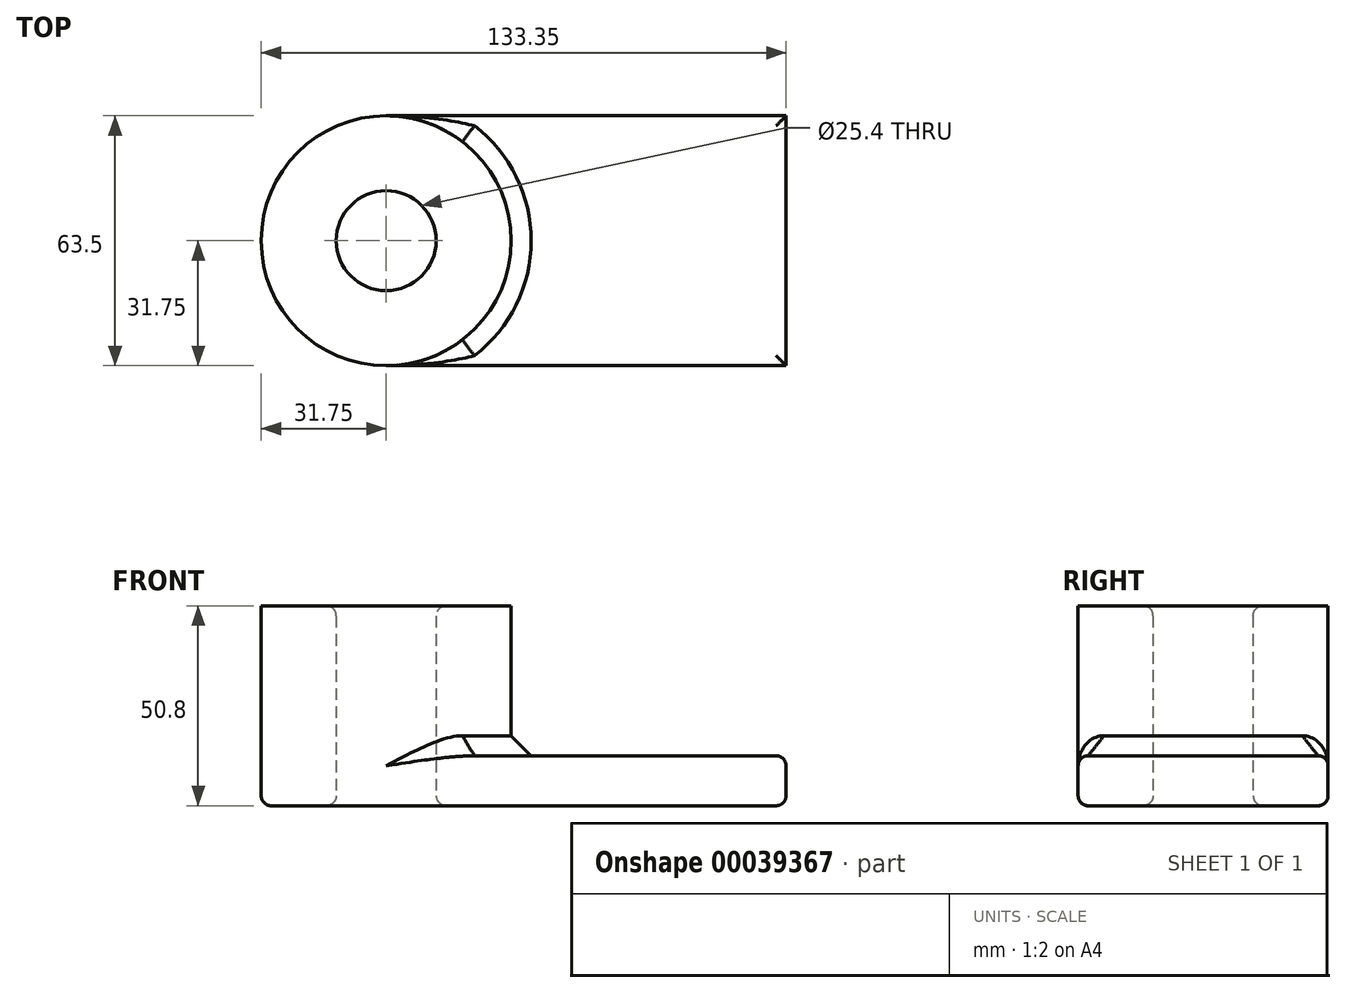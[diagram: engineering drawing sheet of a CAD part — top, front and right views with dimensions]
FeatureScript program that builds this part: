
annotation { "Feature Type Name" : "Feature", "Feature Type Description" : "" }
export const myFeature = defineFeature(function(context is Context, id is Id, definition is map)
    precondition{}
    {
        {
            var Q0;
            Q0=qCreatedBy(makeId("Top.planeOp"),FACE);
            var sketch = newSketch(context, id + "F0", { "sketchPlane" : qUnion([Q0])});
            skLineSegment(sketch, "E0.rect.bottom", {"start": v(50.8, -31.75) * mm, "end": v(-50.8, -31.75) * mm});
            skLineSegment(sketch, "E0.rect.top", {"start": v(50.8, 31.75) * mm, "end": v(-50.8, 31.75) * mm});
            skLineSegment(sketch, "E0.rect.left", {"start": v(50.8, -31.75) * mm, "end": v(50.8, 31.75) * mm});
            skLineSegment(sketch, "E0.rect.right", {"start": v(-50.8, -31.75) * mm, "end": v(-50.8, 31.75) * mm});
            skPoint(sketch, "E0.rect.middle", {"position": v(0, 0) * mm});
            skCircle(sketch, "E1", {"center": v(-50.8, 0) * mm, "radius": 31.75 * mm});
            skCircle(sketch, "E2", {"center": v(-50.8, 0) * mm, "radius": 12.7 * mm});
            skSolve(sketch);
        }
        {
            var Q0;
            {var subQ0=sQuery(id+"F0.wireOp",EDGE,"E2");var subQ1=sQuery(id+"F0.wireOp",EDGE,"E0.rect.right");var subQ3=makeQuery(id+"F0.imprint","INTERSECT",VERTEX,{"disambiguationData":[OD(0.0)],"derivedFrom":[subQ1,subQ0]});Q0=makeQuery(id+"F0.imprint","IMPRINT",FACE,{"disambiguationData":[TD([[makeQuery(id+"F0.imprint","IMPRINT",EDGE,{"disambiguationData":[TD([[subQ3,-1.0]])],"derivedFrom":subQ0}),-1.0]])]});}
            var Q1;
            {var subQ0=sQuery(id+"F0.wireOp",EDGE,"E2");var subQ1=sQuery(id+"F0.wireOp",EDGE,"E0.rect.right");var subQ3=makeQuery(id+"F0.imprint","INTERSECT",VERTEX,{"disambiguationData":[OD(0.0)],"derivedFrom":[subQ1,subQ0]});Q1=makeQuery(id+"F0.imprint","IMPRINT",FACE,{"disambiguationData":[TD([[makeQuery(id+"F0.imprint","IMPRINT",EDGE,{"disambiguationData":[TD([[subQ3,1.0]])],"derivedFrom":subQ0}),-1.0]])]});}
            extrude(context, id + "F1", {"entities" : qUnion([Q0, Q1]), "depth" : 50.8 * mm});
        }
        {
            var Q0;
            Q0 = qSketchRegion(id + "F0", true);
            extrude(context, id + "F2", {"entities" : qUnion([Q0]), "operationType" : NewBodyOperationType.ADD, "depth" : 12.7 * mm});
        }
        {
            var Q0;
            Q0=makeQuery(id+"F1.opExtrude","CAP_EDGE",EDGE,{"disambiguationData":[OSD([sQuery(id+"F0.wireOp",EDGE,"E2")])],"isStart":false});
            var Q1;
            Q1=makeQuery(id+"F2.opExtrude","CAP_EDGE",EDGE,{"disambiguationData":[OSD([sQuery(id+"F0.wireOp",EDGE,"E0.rect.left")])],"isStart":false});
            var Q2;
            Q2=makeQuery(id+"F2.opExtrude","CAP_EDGE",EDGE,{"disambiguationData":[OSD([sQuery(id+"F0.wireOp",EDGE,"E0.rect.bottom")])],"isStart":false});
            var Q3;
            Q3=makeQuery(id+"F1.opExtrude","CAP_EDGE",EDGE,{"disambiguationData":[OSD([sQuery(id+"F0.wireOp",EDGE,"E2")])],"isStart":true});
            var Q4;
            Q4=makeQuery(id+"F1.opExtrude","CAP_EDGE",EDGE,{"disambiguationData":[OSD([sQuery(id+"F0.wireOp",EDGE,"E1")])],"isStart":true});
            var Q5;
            Q5=makeQuery(id+"F2.opExtrude","CAP_EDGE",EDGE,{"disambiguationData":[OSD([sQuery(id+"F0.wireOp",EDGE,"E0.rect.top")])],"isStart":false});
            var Q6;
            Q6=makeQuery(id+"F2.opExtrude","CAP_EDGE",EDGE,{"disambiguationData":[OSD([sQuery(id+"F0.wireOp",EDGE,"E0.rect.left")])],"isStart":true});
            fillet(context, id + "F3", {"entities" : qUnion([Q0, Q1, Q2, Q3, Q4, Q5, Q6]), "radius" : 2.54 * mm, "tangentPropagation" : true, "allowEdgeOverflow" : false});
        }
        {
            var Q0;
            {var subQ0=sQuery(id+"F0.wireOp",EDGE,"E1");Q0=makeQuery(id+"F2.boolean.opBoolean","INTERSECT",EDGE,{"derivedFrom":[makeQuery(id+"F1.opExtrude","SWEPT_FACE",FACE,{"disambiguationData":[OSD([subQ0])]}),makeQuery(id+"F2.opExtrude","CAP_FACE",FACE,{"disambiguationData":[OSD([sQuery(id+"F0.wireOp",EDGE,"E0.rect.bottom"),sQuery(id+"F0.wireOp",EDGE,"E0.rect.top"),sQuery(id+"F0.wireOp",EDGE,"E0.rect.left"),subQ0,sQuery(id+"F0.wireOp",EDGE,"E2")])],"isStart":false})]});}
            chamfer(context, id + "F4", {"entities" : qUnion([Q0]), "width" : 5.08 * mm, "tangentPropagation" : true});
        }
    });
